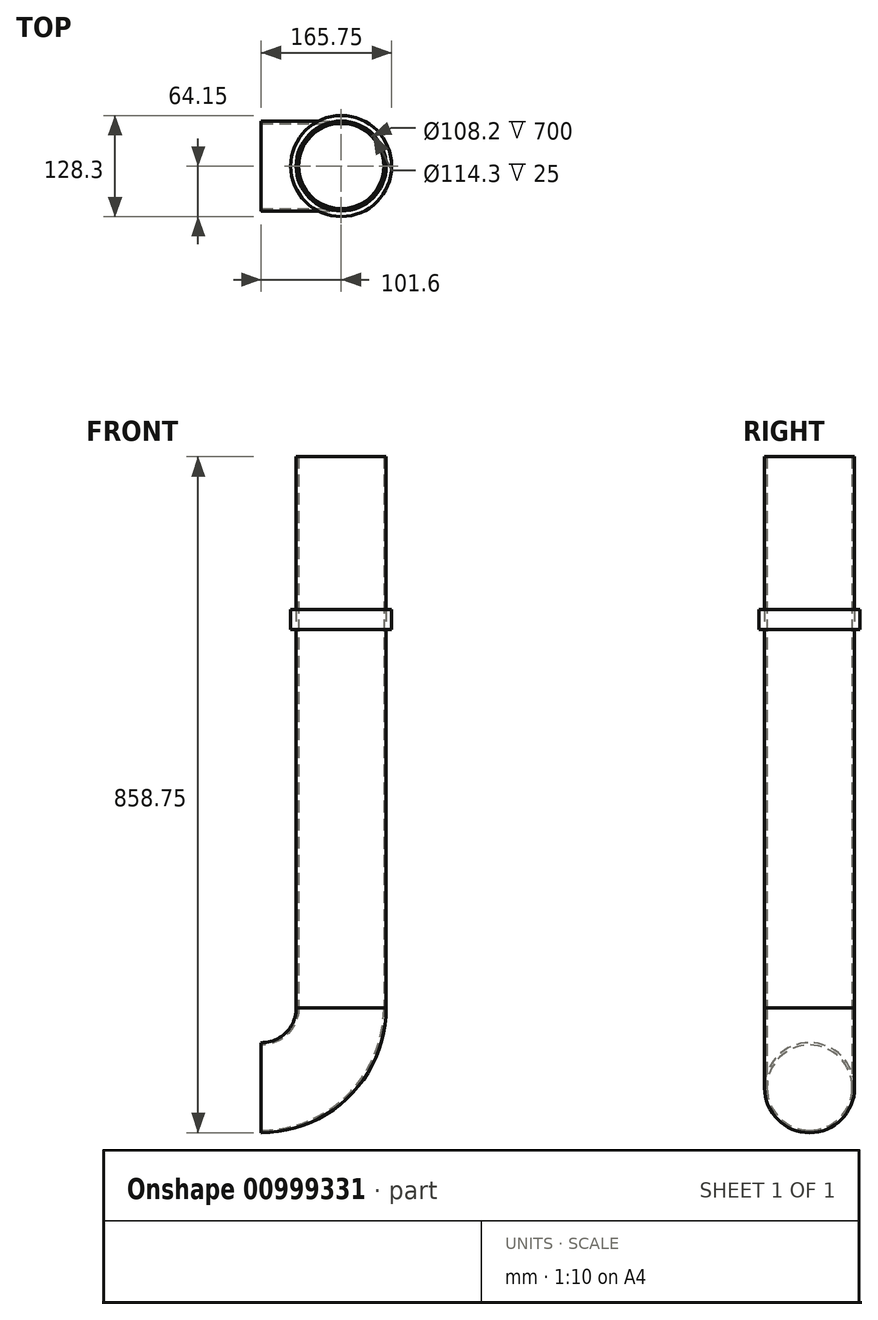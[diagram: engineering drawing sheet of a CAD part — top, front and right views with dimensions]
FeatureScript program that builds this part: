
annotation { "Feature Type Name" : "Feature", "Feature Type Description" : "" }
export const myFeature = defineFeature(function(context is Context, id is Id, definition is map)
    precondition{}
    {
        {
            var Q0;
            Q0=qCreatedBy(makeId("Right.planeOp"),FACE);
            var sketch = newSketch(context, id + "F0", { "sketchPlane" : qUnion([Q0])});
            skCircle(sketch, "E0", {"center": v(0, 0) * mm, "radius": 57.15 * mm});
            skCircle(sketch, "E1", {"center": v(0, 0) * mm, "radius": 54.1 * mm});
            skSolve(sketch);
        }
        {
            var Q0;
            Q0=qCreatedBy(makeId("Front.planeOp"),FACE);
            var sketch = newSketch(context, id + "F1", { "sketchPlane" : qUnion([Q0])});
            skLineSegment(sketch, "E2", {"start": v(0, 0) * mm, "end": v(0, 0) * mm});
            skLineSegment(sketch, "E3", {"start": v(-101.6, 101.6) * mm, "end": v(-101.6, 101.6) * mm});
            skPoint(sketch, "E4.visualSharp", {"position": v(-101.6, 0) * mm});
            skArc(sketch, "E4.filletArc", {"start": v(-101.6, 101.6) * mm, "mid": v(-71.84, 29.76) * mm, "end": v(0, 0) * mm});
            skSolve(sketch);
        }
        {
            var Q0;
            Q0 = qSketchRegion(id + "F0", true);
            extrude(context, id + "F2", {"entities" : qUnion([Q0]), "depth" : 25 * mm, "offsetDistance" : 25 * mm});
        }
        {
            var Q0;
            Q0=makeQuery(id+"F2.opExtrude","CAP_FACE",FACE,{"disambiguationData":[OSD([sQuery(id+"F0.wireOp",EDGE,"E0"),sQuery(id+"F0.wireOp",EDGE,"E1")])],"isStart":true});
            var sketch = newSketch(context, id + "F3", { "sketchPlane" : qUnion([Q0])});
            skLineSegment(sketch, "E5", {"start": v(0, 0) * mm, "end": v(-57.15, 0) * mm});
            skSolve(sketch);
        }
        {
            var Q0;
            Q0=makeQuery(id+"F3.imprint","IMPRINT",FACE,{"disambiguationData":[TD([[makeQuery(id+"F3.imprint","IMPRINT",EDGE,{"derivedFrom":makeQuery(id+"F2.opExtrude","CAP_EDGE",EDGE,{"disambiguationData":[OSD([sQuery(id+"F0.wireOp",EDGE,"E0")])],"isStart":true})}),-1.0]])]});
            var Q1;
            Q1=sQuery(id+"F1.wireOp",EDGE,"E4.filletArc");
            sweep(context, id + "F4", {"profiles" : qUnion([Q0]), "path" : qUnion([Q1])});
        }
        {
            var Q0;
            Q0=makeQuery(id+"F2.opExtrude","SWEPT_BODY",BODY,{"disambiguationData":[OSD([sQuery(id+"F0.wireOp",EDGE,"E0"),sQuery(id+"F0.wireOp",EDGE,"E1")])]});
            deleteBodies(context, id + "F5", {"entities" : qUnion([Q0])});
        }
        {
            var Q0;
            Q0=makeQuery(id+"F4.opSweep","CAP_FACE",FACE,{"disambiguationData":[OSD([sQuery(id+"F0.wireOp",EDGE,"E0"),sQuery(id+"F0.wireOp",EDGE,"E1"),sQuery(id+"F1.wireOp",VERTEX,"E4.filletArc.start")])],"isStart":false});
            extrude(context, id + "F6", {"entities" : qUnion([Q0]), "depth" : 700 * mm, "offsetDistance" : 25 * mm});
        }
        {
            var Q0;
            Q0=makeQuery(id+"F6.opExtrude","SWEPT_BODY",BODY,{"disambiguationData":[OSD([sQuery(id+"F0.wireOp",EDGE,"E0"),sQuery(id+"F0.wireOp",EDGE,"E1"),sQuery(id+"F1.wireOp",VERTEX,"E4.filletArc.start")])]});
            var Q1;
            Q1=makeQuery(id+"F4.opSweep","SWEPT_BODY",BODY,{"disambiguationData":[OSD([sQuery(id+"F0.wireOp",EDGE,"E0"),sQuery(id+"F0.wireOp",EDGE,"E1"),sQuery(id+"F1.wireOp",EDGE,"E4.filletArc")])]});
            var Q2;
            Q2=makeQuery(id+"F6.opExtrude","CAP_EDGE",EDGE,{"disambiguationData":[OSD([sQuery(id+"F0.wireOp",EDGE,"E1"),sQuery(id+"F1.wireOp",VERTEX,"E4.filletArc.start")])],"isStart":false});
            transform(context, id + "F7", {"entities" : qUnion([Q0, Q1]), "transformType" : TransformType.ROTATION, "transformAxis" : qUnion([Q2]), "angle" : 180 * degree, "makeCopy" : false});
        }
        {
            var Q0;
            Q0=makeQuery(id+"F6.opExtrude","CAP_FACE",FACE,{"disambiguationData":[OSD([sQuery(id+"F0.wireOp",EDGE,"E0"),sQuery(id+"F0.wireOp",EDGE,"E1"),sQuery(id+"F1.wireOp",VERTEX,"E4.filletArc.start")])],"isStart":false});
            var sketch = newSketch(context, id + "F8", { "sketchPlane" : qUnion([Q0])});
            skCircle(sketch, "E6", {"center": v(-101.6, 0) * mm, "radius": 64.15 * mm});
            skCircle(sketch, "E7", {"center": v(-101.6, 0) * mm, "radius": 57.15 * mm});
            skSolve(sketch);
        }
        {
            var Q0;
            Q0 = qSketchRegion(id + "F8", true);
            extrude(context, id + "F9", {"entities" : qUnion([Q0]), "oppositeDirection" : true, "depth" : 25 * mm, "offsetDistance" : 25 * mm});
        }
        {
            var Q0;
            Q0=makeQuery(id+"F9.opExtrude","SWEPT_BODY",BODY,{"disambiguationData":[OSD([sQuery(id+"F8.wireOp",EDGE,"E6"),sQuery(id+"F8.wireOp",EDGE,"E7")])]});
            transform(context, id + "F10", {"entities" : qUnion([Q0]), "transformType" : TransformType.TRANSLATION_3D, "dx" : 0 * mm, "dy" : 0 * mm, "dz" : -194.45 * mm, "makeCopy" : false});
        }
    });
